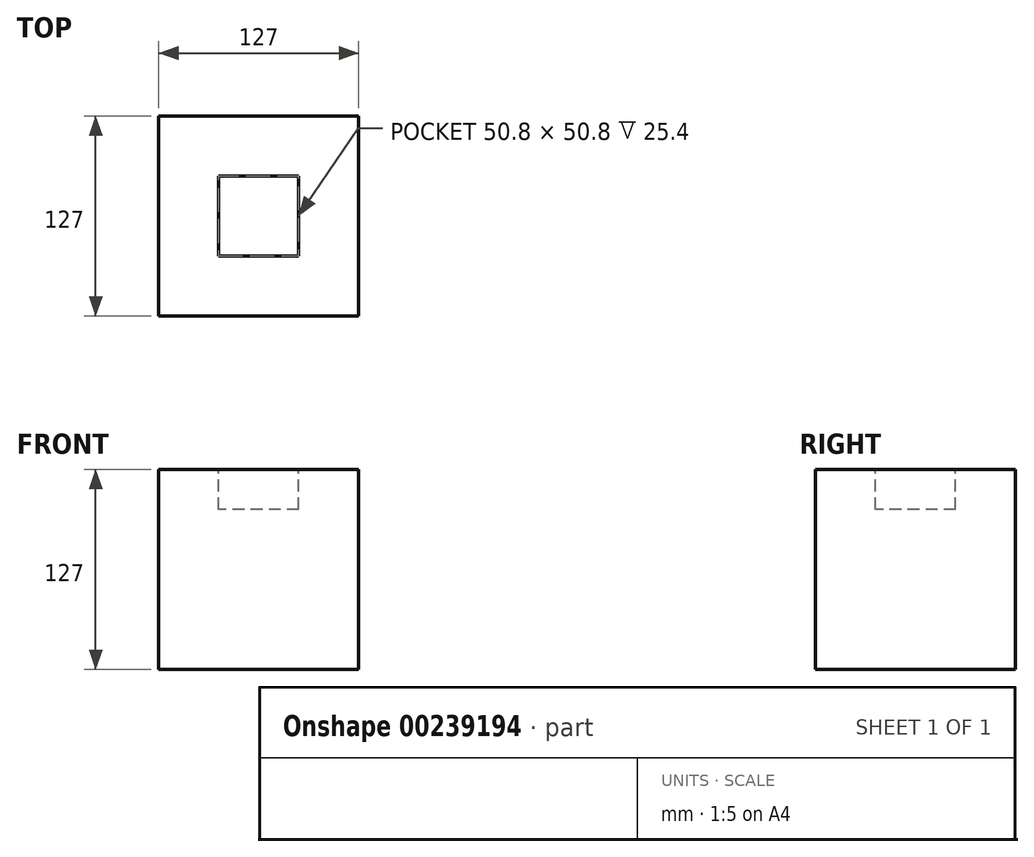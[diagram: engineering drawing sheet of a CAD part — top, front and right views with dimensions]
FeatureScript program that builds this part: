
annotation { "Feature Type Name" : "Feature", "Feature Type Description" : "" }
export const myFeature = defineFeature(function(context is Context, id is Id, definition is map)
    precondition{}
    {
        {
            var Q0;
            Q0=qCreatedBy(makeId("Front.planeOp"),FACE);
            var sketch = newSketch(context, id + "F0", { "sketchPlane" : qUnion([Q0])});
            skLineSegment(sketch, "E0.bottom", {"start": v(-63.5, 63.5) * mm, "end": v(63.5, 63.5) * mm});
            skLineSegment(sketch, "E0.top", {"start": v(-63.5, -63.5) * mm, "end": v(63.5, -63.5) * mm});
            skLineSegment(sketch, "E0.left", {"start": v(-63.5, 63.5) * mm, "end": v(-63.5, -63.5) * mm});
            skLineSegment(sketch, "E0.right", {"start": v(63.5, 63.5) * mm, "end": v(63.5, -63.5) * mm});
            skSolve(sketch);
        }
        {
            var Q0;
            Q0=makeQuery(id+"F0.imprint","IMPRINT",FACE,{"disambiguationData":[TD([[makeQuery(id+"F0.imprint","IMPRINT",EDGE,{"derivedFrom":sQuery(id+"F0.wireOp",EDGE,"E0.bottom")}),-1.0]])]});
            extrude(context, id + "F1", {"entities" : qUnion([Q0]), "endBound" : BoundingType.SYMMETRIC, "depth" : 127 * mm});
        }
        {
            var Q0;
            Q0=makeQuery(id+"F1.opExtrude","SWEPT_FACE",FACE,{"disambiguationData":[OSD([sQuery(id+"F0.wireOp",EDGE,"E0.bottom")])]});
            var sketch = newSketch(context, id + "F2", { "sketchPlane" : qUnion([Q0])});
            skLineSegment(sketch, "E1.bottom", {"start": v(25.4, 25.4) * mm, "end": v(-25.4, 25.4) * mm});
            skLineSegment(sketch, "E1.top", {"start": v(25.4, -25.4) * mm, "end": v(-25.4, -25.4) * mm});
            skLineSegment(sketch, "E1.left", {"start": v(25.4, 25.4) * mm, "end": v(25.4, -25.4) * mm});
            skLineSegment(sketch, "E1.right", {"start": v(-25.4, 25.4) * mm, "end": v(-25.4, -25.4) * mm});
            skPoint(sketch, "E1.middle", {"position": v(0, 0) * mm});
            skSolve(sketch);
        }
        {
            var Q0;
            Q0 = qSketchRegion(id + "F2", true);
            extrude(context, id + "F3", {"entities" : qUnion([Q0]), "operationType" : NewBodyOperationType.REMOVE, "oppositeDirection" : true, "depth" : 25.4 * mm});
        }
    });
